# Revit family: Ventüer_VentilationLouvres_VL-100CM
name_source: partatom
category: Generic Models
units: mm (PartAtom-declared; Revit-internal decimal feet)

## family parameters
Always vertical = No
Can host rebar = No
Cut with Voids When Loaded = No
Part Type = Normal
Room Calculation Point = No
Round Connector Dimension = Use Diameter
Shared = No
Work Plane-Based = Yes

## types (4) — shared parameters
Aerodynamic Performance = Air Inlet: 0.351, Class 2. Air Extract: 0.370, Class 2
Ancillaries = Bird Mesh, Insect Mesh, Solid Blanking, Perimeter Mounting Angle
Blade Centres = 100 mm  [stored 0.328084 ft]
Blade Count = 5
Blade Cut Offset = 500 mm  [stored 1.64042 ft]
Blade Material = Ventüer Aluminium
Clip Multiple Transition = No
Clip Single Transition = Yes
Clip Transition Count = 3
Default Elevation = 1219 mm
Description = Cost-Effective Visual Screening
Exact Neck Height = 594 mm  [stored 1.94882 ft]
Exact Neck Height Check = 594 mm  [stored 1.94882 ft]
Exact Neck Width = 594 mm  [stored 1.94882 ft]
Exact Neck Width Check = 594 mm  [stored 1.94882 ft]
Frame Material = Ventüer Aluminium
Frame Set Count = 1
Frame Set Count Check = 2
Frame Set Transition Count = 1
Frame Set Transition Count Check = 2
Manufacturer = Ventüer
Max Flow = 5000.0 L/s
Min Flow = 100.0 L/s
Model = VL-100CM
Multiple Frame Set = No
Multiple Transition = No
Noise Level NC Max = 0.00 NC
Noise Level NC Min = 0.00 NC
Nominal Height = 600 mm
Nominal Width = 600 mm
Nominated Air Flow = 100.0 L/s
Nominated Pessure Drop = 21.0 Pa
Post Depth = 200 mm
Post Width = 100 mm  [stored 0.328084 ft]
Rain Defence Performance = Class C - up to 0.5m/s suction velocity. Class D - up to 3.5m/s suction velocity
Single Transition = No
Specified Air Flow = 0.0 L/s
Specified Pressure Drop = 21.0 Pa
Static Pressure Max = 60.0 Pa
Static Pressure Min = 10.0 Pa
URL = https://www.ventuer.co
Ventüer Product Range = Ventilation Louvres

## per-type parameters (varying)
- VL-100CM_CF: Base Width=26 mm; Blade And Frame Gap=9 mm  [stored 0.0295276 ft]; Channel=Yes; Clip=No; Clip Blade Count=10; Clip Height=516 mm; Clip Width=574 mm; Connector Height=558 mm  [stored 1.83071 ft]; Connector Width=574 mm; Depth=150 mm; Flanged=No; Frame Set Height=558 mm  [stored 1.83071 ft]; Frame Set Width=574 mm; Glazed=No; Keynote=VL-100CM_FF; Overall Opening Height=558 mm  [stored 1.83071 ft]; Overall Opening Width=574 mm; Profile Width=10 mm  [stored 0.0328084 ft]; Rear Frame Set Offset=11 mm; Rear Mullion Offset=1 mm  [stored 0.00328084 ft]; Single Frame Set=Yes; Single Frame Set Width=287 mm; Support And Frame Gap=16 mm  [stored 0.0524934 ft]; Support Centres=50 mm  [stored 0.164042 ft]; Top Blade=Yes; Top Blade Height=56 mm; Top Support Corrector=14 mm  [stored 0.0459318 ft]; Top Support Height=42 mm  [stored 0.137795 ft]
- VL-100CM_GF: Base Width=26 mm; Blade And Frame Gap=10 mm  [stored 0.0328084 ft]; Channel=No; Clip=No; Clip Blade Count=10; Clip Height=517 mm; Clip Width=542 mm; Connector Height=542 mm; Connector Width=542 mm; Depth=155 mm; Flanged=No; Frame Set Height=542 mm; Frame Set Width=542 mm; Glazed=Yes; Keynote=VL-100CM_GF; Overall Opening Height=542 mm; Overall Opening Width=542 mm; Profile Width=26 mm; Rear Frame Set Offset=13 mm; Rear Mullion Offset=1 mm  [stored 0.00328084 ft]; Single Frame Set=Yes; Single Frame Set Width=271 mm; Support And Frame Gap=17 mm; Support Centres=100 mm  [stored 0.328084 ft]; Top Blade=Yes; Top Blade Height=32 mm; Top Support Corrector=7 mm  [stored 0.0229659 ft]; Top Support Height=25 mm  [stored 0.082021 ft]
- VL-100CM_FF: Base Width=25 mm  [stored 0.082021 ft]; Blade And Frame Gap=10 mm  [stored 0.0328084 ft]; Channel=No; Clip=No; Clip Blade Count=10; Clip Height=517 mm; Clip Width=544 mm  [stored 1.78478 ft]; Connector Height=544 mm  [stored 1.78478 ft]; Connector Width=544 mm  [stored 1.78478 ft]; Depth=160 mm  [stored 0.524934 ft]; Flanged=Yes; Frame Set Height=544 mm  [stored 1.78478 ft]; Frame Set Width=544 mm  [stored 1.78478 ft]; Glazed=No; Keynote=VL-100CM_FF; Overall Opening Height=544 mm  [stored 1.78478 ft]; Overall Opening Width=544 mm  [stored 1.78478 ft]; Profile Width=25 mm  [stored 0.082021 ft]; Rear Frame Set Offset=16 mm  [stored 0.0524934 ft]; Rear Mullion Offset=1 mm  [stored 0.00328084 ft]; Single Frame Set=Yes; Single Frame Set Width=272 mm; Support And Frame Gap=17 mm; Support Centres=100 mm  [stored 0.328084 ft]; Top Blade=Yes; Top Blade Height=34 mm; Top Support Corrector=7 mm  [stored 0.0229659 ft]; Top Support Height=27 mm
- VL-100CM_Clip: Base Width=0 mm  [stored 0 ft]; Blade And Frame Gap=10 mm  [stored 0.0328084 ft]; Channel=No; Clip=Yes; Clip Blade Count=11; Clip Height=517 mm; Clip Width=594 mm  [stored 1.94882 ft]; Connector Height=594 mm  [stored 1.94882 ft]; Connector Width=594 mm  [stored 1.94882 ft]; Depth=160 mm  [stored 0.524934 ft]; Flanged=No; Frame Set Height=594 mm  [stored 1.94882 ft]; Frame Set Width=594 mm  [stored 1.94882 ft]; Glazed=No; Keynote=VL-100CM_Clip; Overall Opening Height=594 mm  [stored 1.94882 ft]; Overall Opening Width=594 mm  [stored 1.94882 ft]; Profile Width=0 mm  [stored 0 ft]; Rear Frame Set Offset=16 mm  [stored 0.0524934 ft]; Rear Mullion Offset=21 mm; Single Frame Set=No; Single Frame Set Width=297 mm  [stored 0.974409 ft]; Support And Frame Gap=17 mm; Support Centres=50 mm  [stored 0.164042 ft]; Top Blade=No; Top Blade Height=84 mm; Top Support Corrector=7 mm  [stored 0.0229659 ft]; Top Support Height=27 mm

note: [stored X ft] marks values corroborated as IEEE doubles in the binary element streams (Revit-internal decimal feet)

## geometry (parser evidence)
native form markers: Sweep x39
no freeform markers — native parametric forms only
